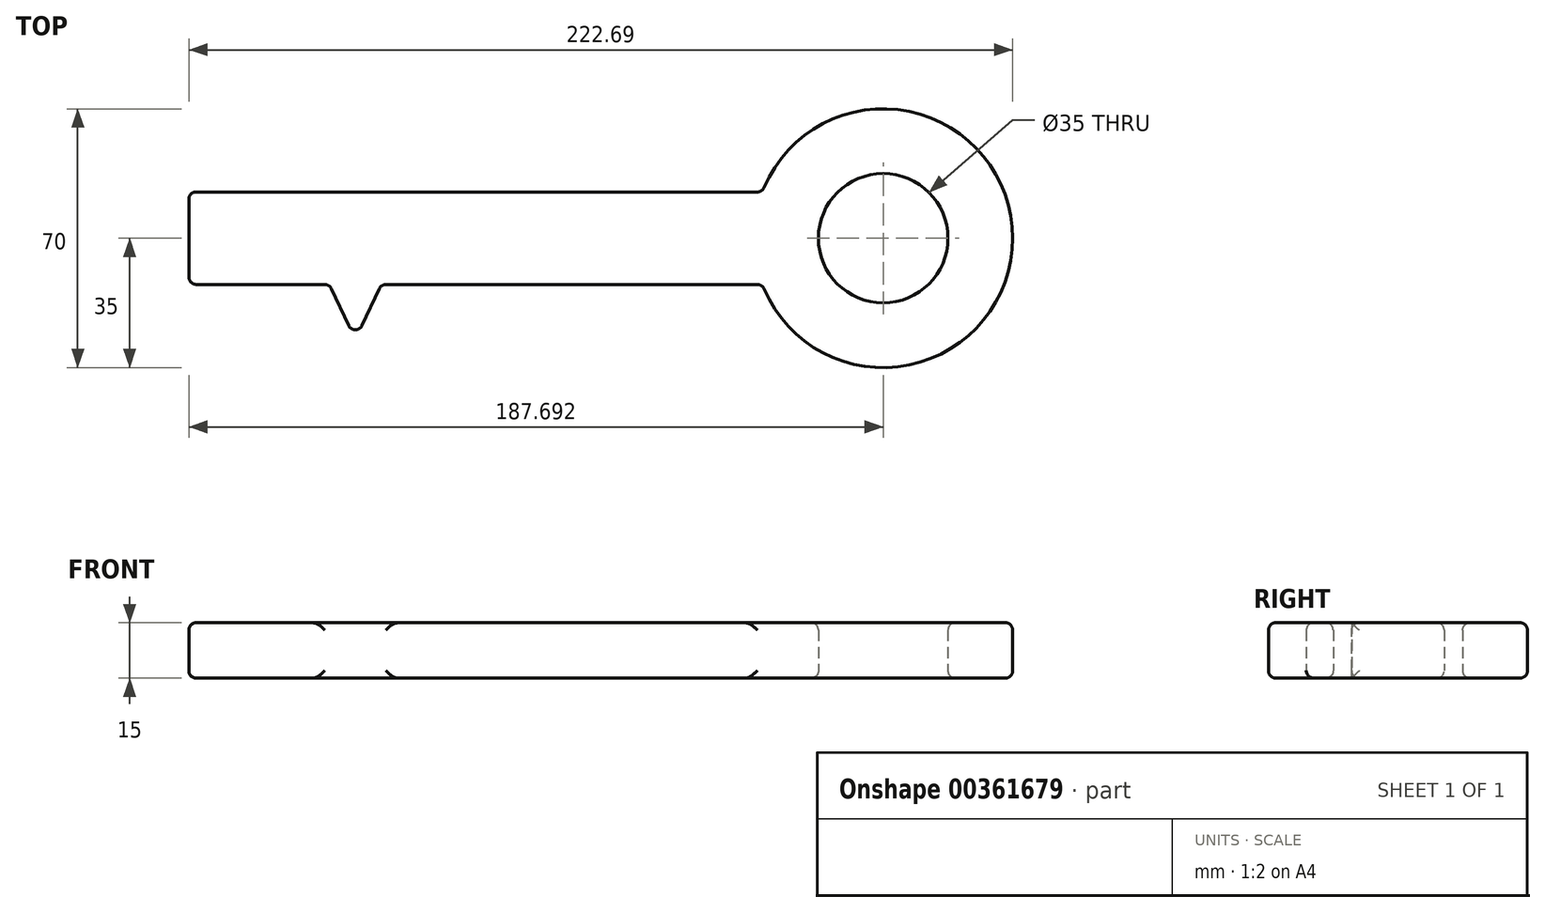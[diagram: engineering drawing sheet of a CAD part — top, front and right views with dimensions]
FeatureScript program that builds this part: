
annotation { "Feature Type Name" : "Feature", "Feature Type Description" : "" }
export const myFeature = defineFeature(function(context is Context, id is Id, definition is map)
    precondition{}
    {
        {
            var Q0;
            Q0=qCreatedBy(makeId("Top.planeOp"),FACE);
            var sketch = newSketch(context, id + "F0", { "sketchPlane" : qUnion([Q0])});
            skLineSegment(sketch, "E0.bottom", {"start": v(-10, 14.65) * mm, "end": v(145, 14.65) * mm});
            skLineSegment(sketch, "E0.top", {"start": v(-10, -10.35) * mm, "end": v(145, -10.35) * mm});
            skLineSegment(sketch, "E0.left", {"start": v(-10, 14.65) * mm, "end": v(-10, -10.35) * mm});
            skLineSegment(sketch, "E1.bottom", {"start": v(0, -10.35) * mm, "end": v(-10, -10.35) * mm});
            skLineSegment(sketch, "E1.top", {"start": v(0, -40.35) * mm, "end": v(-10, -40.35) * mm});
            skLineSegment(sketch, "E1.left", {"start": v(-10, -40.35) * mm, "end": v(-10, -10.35) * mm});
            skLineSegment(sketch, "E1.right", {"start": v(0, -40.35) * mm, "end": v(0, -10.35) * mm});
            skLineSegment(sketch, "E2.top", {"start": v(0, -10.35) * mm, "end": v(145, -10.35) * mm});
            skLineSegment(sketch, "E3.bottom", {"start": v(10, -10.35) * mm, "end": v(18, -10.35) * mm});
            skLineSegment(sketch, "E3.top", {"start": v(10, -10.35) * mm, "end": v(18, -10.35) * mm});
            skLineSegment(sketch, "E3.left", {"start": v(10, -10.35) * mm, "end": v(10, -10.35) * mm});
            skLineSegment(sketch, "E3.right", {"start": v(18, -10.35) * mm, "end": v(18, -10.35) * mm});
            skLineSegment(sketch, "E4.top", {"start": v(10, -25.35) * mm, "end": v(18, -25.35) * mm});
            skLineSegment(sketch, "E4.left", {"start": v(10, -10.35) * mm, "end": v(10, -25.35) * mm});
            skLineSegment(sketch, "E4.right", {"start": v(18, -10.35) * mm, "end": v(18, -25.35) * mm});
            skLineSegment(sketch, "E5", {"start": v(28, -10.35) * mm, "end": v(35, -25.35) * mm});
            skLineSegment(sketch, "E6", {"start": v(35, -25.35) * mm, "end": v(42, -10.35) * mm});
            skArc(sketch, "E7", {"start": v(145, -10.35) * mm, "mid": v(212.7, 2.15) * mm, "end": v(145, 14.65) * mm});
            skCircle(sketch, "E8", {"center": v(177.7, 2.15) * mm, "radius": 17.5 * mm});
            skLineSegment(sketch, "E9", {"start": v(177.7, 2.15) * mm, "end": v(-10, 2.15) * mm, "construction": true});
            skSolve(sketch);
        }
        {
            var Q0;
            {var subQ0=sQuery(id+"F0.wireOp",EDGE,"E5");Q0=makeQuery(id+"F0.imprint","IMPRINT",FACE,{"disambiguationData":[TD([[makeQuery(id+"F0.imprint","IMPRINT",EDGE,{"derivedFrom":subQ0}),1.0]])]});}
            var Q1;
            Q1=makeQuery(id+"F0.imprint","IMPRINT",FACE,{"disambiguationData":[TD([[makeQuery(id+"F0.imprint","IMPRINT",EDGE,{"derivedFrom":sQuery(id+"F0.wireOp",EDGE,"E1.bottom")}),1.0]])]});
            var Q2;
            Q2=makeQuery(id+"F0.imprint","IMPRINT",FACE,{"disambiguationData":[TD([[makeQuery(id+"F0.imprint","IMPRINT",EDGE,{"derivedFrom":sQuery(id+"F0.wireOp",EDGE,"E0.bottom")}),-1.0]])]});
            var Q3;
            Q3=makeQuery(id+"F0.imprint","IMPRINT",FACE,{"disambiguationData":[TD([[makeQuery(id+"F0.imprint","IMPRINT",EDGE,{"derivedFrom":sQuery(id+"F0.wireOp",EDGE,"E3.bottom")}),-1.0]])]});
            extrude(context, id + "F1", {"entities" : qUnion([Q0, Q1, Q2, Q3]), "depth" : 15 * mm});
        }
        {
            var Q0;
            Q0=makeQuery(id+"F1.opExtrude","CAP_EDGE",EDGE,{"disambiguationData":[OSD([sQuery(id+"F0.wireOp",EDGE,"E6")])],"isStart":true});
            var Q1;
            Q1=makeQuery(id+"F1.opExtrude","CAP_EDGE",EDGE,{"disambiguationData":[OSD([sQuery(id+"F0.wireOp",EDGE,"E8")])],"isStart":true});
            var Q2;
            Q2=makeQuery(id+"F1.opExtrude","CAP_EDGE",EDGE,{"disambiguationData":[OSD([sQuery(id+"F0.wireOp",EDGE,"E5")])],"isStart":true});
            var Q3;
            {var subQ0=sQuery(id+"F0.wireOp",EDGE,"E2.top");Q3=makeQuery(id+"F1.opExtrude","CAP_EDGE",EDGE,{"disambiguationData":[OSD([subQ0]),TDD([makeQuery(id+"F0.imprint","IMPRINT",EDGE,{"disambiguationData":[TD([[makeQuery(id+"F0.imprint","INTERSECT",VERTEX,{"derivedFrom":[subQ0,sQuery(id+"F0.wireOp",EDGE,"E5")]}),1.0]])],"derivedFrom":subQ0})])],"isStart":true});}
            var Q4;
            Q4=makeQuery(id+"F1.opExtrude","SWEPT_EDGE",EDGE,{"disambiguationData":[OSD([sQuery(id+"F0.wireOp",EDGE,"E2.top"),sQuery(id+"F0.wireOp",EDGE,"E5")])]});
            var Q5;
            Q5=makeQuery(id+"F1.opExtrude","CAP_EDGE",EDGE,{"disambiguationData":[OSD([sQuery(id+"F0.wireOp",EDGE,"E4.top")])],"isStart":true});
            var Q6;
            {var subQ0=sQuery(id+"F0.wireOp",EDGE,"E2.top");Q6=makeQuery(id+"F1.opExtrude","CAP_EDGE",EDGE,{"disambiguationData":[OSD([subQ0]),TDD([makeQuery(id+"F0.imprint","IMPRINT",EDGE,{"disambiguationData":[TD([[makeQuery(id+"F0.imprint","INTERSECT",VERTEX,{"derivedFrom":[subQ0,sQuery(id+"F0.wireOp",EDGE,"E7")]}),1.0]])],"derivedFrom":subQ0})])],"isStart":true});}
            var Q7;
            Q7=makeQuery(id+"F1.opExtrude","CAP_EDGE",EDGE,{"disambiguationData":[OSD([sQuery(id+"F0.wireOp",EDGE,"E8")])],"isStart":false});
            var Q8;
            Q8=makeQuery(id+"F1.opExtrude","SWEPT_EDGE",EDGE,{"disambiguationData":[OSD([sQuery(id+"F0.wireOp",EDGE,"E2.top"),sQuery(id+"F0.wireOp",EDGE,"E6")])]});
            var Q9;
            Q9=makeQuery(id+"F1.opExtrude","CAP_EDGE",EDGE,{"disambiguationData":[OSD([sQuery(id+"F0.wireOp",EDGE,"E1.right")])],"isStart":true});
            var Q10;
            Q10=makeQuery(id+"F1.opExtrude","CAP_EDGE",EDGE,{"disambiguationData":[OSD([sQuery(id+"F0.wireOp",EDGE,"E4.right")])],"isStart":true});
            var Q11;
            Q11=makeQuery(id+"F1.opExtrude","SWEPT_EDGE",EDGE,{"disambiguationData":[OSD([sQuery(id+"F0.wireOp",EDGE,"E5"),sQuery(id+"F0.wireOp",EDGE,"E6")])]});
            var Q12;
            Q12=makeQuery(id+"F1.opExtrude","SWEPT_EDGE",EDGE,{"disambiguationData":[OSD([sQuery(id+"F0.wireOp",EDGE,"E2.top"),sQuery(id+"F0.wireOp",EDGE,"E3.bottom"),sQuery(id+"F0.wireOp",EDGE,"E4.left")])]});
            var Q13;
            Q13=makeQuery(id+"F1.opExtrude","SWEPT_EDGE",EDGE,{"disambiguationData":[OSD([sQuery(id+"F0.wireOp",EDGE,"E1.bottom"),sQuery(id+"F0.wireOp",EDGE,"E1.right"),sQuery(id+"F0.wireOp",EDGE,"E2.top")])]});
            var Q14;
            Q14=makeQuery(id+"F1.opExtrude","CAP_EDGE",EDGE,{"disambiguationData":[OSD([sQuery(id+"F0.wireOp",EDGE,"E6")])],"isStart":false});
            var Q15;
            Q15=makeQuery(id+"F1.opExtrude","SWEPT_EDGE",EDGE,{"disambiguationData":[OSD([sQuery(id+"F0.wireOp",EDGE,"E2.top"),sQuery(id+"F0.wireOp",EDGE,"E7")])]});
            var Q16;
            Q16=makeQuery(id+"F1.opExtrude","CAP_EDGE",EDGE,{"disambiguationData":[OSD([sQuery(id+"F0.wireOp",EDGE,"E0.bottom")])],"isStart":true});
            var Q17;
            Q17=makeQuery(id+"F1.opExtrude","SWEPT_EDGE",EDGE,{"disambiguationData":[OSD([sQuery(id+"F0.wireOp",EDGE,"E4.top"),sQuery(id+"F0.wireOp",EDGE,"E4.right")])]});
            var Q18;
            Q18=makeQuery(id+"F1.opExtrude","SWEPT_EDGE",EDGE,{"disambiguationData":[OSD([sQuery(id+"F0.wireOp",EDGE,"E4.top"),sQuery(id+"F0.wireOp",EDGE,"E4.left")])]});
            var Q19;
            Q19=makeQuery(id+"F1.opExtrude","SWEPT_EDGE",EDGE,{"disambiguationData":[OSD([sQuery(id+"F0.wireOp",EDGE,"E2.top"),sQuery(id+"F0.wireOp",EDGE,"E3.bottom"),sQuery(id+"F0.wireOp",EDGE,"E4.right")])]});
            var Q20;
            {var subQ0=sQuery(id+"F0.wireOp",EDGE,"E2.top");Q20=makeQuery(id+"F1.opExtrude","CAP_EDGE",EDGE,{"disambiguationData":[OSD([subQ0]),TDD([makeQuery(id+"F0.imprint","IMPRINT",EDGE,{"disambiguationData":[TD([[makeQuery(id+"F0.imprint","INTERSECT",VERTEX,{"derivedFrom":[sQuery(id+"F0.wireOp",EDGE,"E1.bottom"),sQuery(id+"F0.wireOp",EDGE,"E1.right"),subQ0]}),-1.0]])],"derivedFrom":subQ0})])],"isStart":true});}
            var Q21;
            Q21=makeQuery(id+"F1.opExtrude","CAP_EDGE",EDGE,{"disambiguationData":[OSD([sQuery(id+"F0.wireOp",EDGE,"E4.left")])],"isStart":true});
            var Q22;
            Q22=makeQuery(id+"F1.opExtrude","SWEPT_EDGE",EDGE,{"disambiguationData":[OSD([sQuery(id+"F0.wireOp",EDGE,"E1.top"),sQuery(id+"F0.wireOp",EDGE,"E1.right")])]});
            var Q23;
            Q23=makeQuery(id+"F1.opExtrude","CAP_EDGE",EDGE,{"disambiguationData":[OSD([sQuery(id+"F0.wireOp",EDGE,"E0.left"),sQuery(id+"F0.wireOp",EDGE,"E1.left")])],"isStart":true});
            var Q24;
            Q24=makeQuery(id+"F1.opExtrude","CAP_EDGE",EDGE,{"disambiguationData":[OSD([sQuery(id+"F0.wireOp",EDGE,"E1.top")])],"isStart":true});
            var Q25;
            Q25=makeQuery(id+"F1.opExtrude","CAP_EDGE",EDGE,{"disambiguationData":[OSD([sQuery(id+"F0.wireOp",EDGE,"E5")])],"isStart":false});
            var Q26;
            Q26=makeQuery(id+"F1.opExtrude","SWEPT_EDGE",EDGE,{"disambiguationData":[OSD([sQuery(id+"F0.wireOp",EDGE,"E0.bottom"),sQuery(id+"F0.wireOp",EDGE,"E7")])]});
            var Q27;
            Q27=makeQuery(id+"F1.opExtrude","CAP_EDGE",EDGE,{"disambiguationData":[OSD([sQuery(id+"F0.wireOp",EDGE,"E0.left"),sQuery(id+"F0.wireOp",EDGE,"E1.left")])],"isStart":false});
            var Q28;
            Q28=makeQuery(id+"F1.opExtrude","CAP_EDGE",EDGE,{"disambiguationData":[OSD([sQuery(id+"F0.wireOp",EDGE,"E1.right")])],"isStart":false});
            var Q29;
            {var subQ0=sQuery(id+"F0.wireOp",EDGE,"E2.top");Q29=makeQuery(id+"F1.opExtrude","CAP_EDGE",EDGE,{"disambiguationData":[OSD([subQ0]),TDD([makeQuery(id+"F0.imprint","IMPRINT",EDGE,{"disambiguationData":[TD([[makeQuery(id+"F0.imprint","INTERSECT",VERTEX,{"derivedFrom":[subQ0,sQuery(id+"F0.wireOp",EDGE,"E7")]}),1.0]])],"derivedFrom":subQ0})])],"isStart":false});}
            var Q30;
            Q30=makeQuery(id+"F1.opExtrude","CAP_EDGE",EDGE,{"disambiguationData":[OSD([sQuery(id+"F0.wireOp",EDGE,"E4.top")])],"isStart":false});
            var Q31;
            Q31=makeQuery(id+"F1.opExtrude","CAP_EDGE",EDGE,{"disambiguationData":[OSD([sQuery(id+"F0.wireOp",EDGE,"E4.right")])],"isStart":false});
            var Q32;
            Q32=makeQuery(id+"F1.opExtrude","CAP_EDGE",EDGE,{"disambiguationData":[OSD([sQuery(id+"F0.wireOp",EDGE,"E4.left")])],"isStart":false});
            var Q33;
            {var subQ0=sQuery(id+"F0.wireOp",EDGE,"E2.top");Q33=makeQuery(id+"F1.opExtrude","CAP_EDGE",EDGE,{"disambiguationData":[OSD([subQ0]),TDD([makeQuery(id+"F0.imprint","IMPRINT",EDGE,{"disambiguationData":[TD([[makeQuery(id+"F0.imprint","INTERSECT",VERTEX,{"derivedFrom":[sQuery(id+"F0.wireOp",EDGE,"E1.bottom"),sQuery(id+"F0.wireOp",EDGE,"E1.right"),subQ0]}),-1.0]])],"derivedFrom":subQ0})])],"isStart":false});}
            var Q34;
            Q34=makeQuery(id+"F1.opExtrude","SWEPT_EDGE",EDGE,{"disambiguationData":[OSD([sQuery(id+"F0.wireOp",EDGE,"E1.top"),sQuery(id+"F0.wireOp",EDGE,"E1.left")])]});
            var Q35;
            {var subQ0=sQuery(id+"F0.wireOp",EDGE,"E2.top");Q35=makeQuery(id+"F1.opExtrude","CAP_EDGE",EDGE,{"disambiguationData":[OSD([subQ0]),TDD([makeQuery(id+"F0.imprint","IMPRINT",EDGE,{"disambiguationData":[TD([[makeQuery(id+"F0.imprint","INTERSECT",VERTEX,{"derivedFrom":[subQ0,sQuery(id+"F0.wireOp",EDGE,"E5")]}),1.0]])],"derivedFrom":subQ0})])],"isStart":false});}
            var Q36;
            Q36=makeQuery(id+"F1.opExtrude","SWEPT_EDGE",EDGE,{"disambiguationData":[OSD([sQuery(id+"F0.wireOp",EDGE,"E0.bottom"),sQuery(id+"F0.wireOp",EDGE,"E0.left")])]});
            var Q37;
            Q37=makeQuery(id+"F1.opExtrude","CAP_EDGE",EDGE,{"disambiguationData":[OSD([sQuery(id+"F0.wireOp",EDGE,"E0.bottom")])],"isStart":false});
            var Q38;
            Q38=makeQuery(id+"F1.opExtrude","CAP_EDGE",EDGE,{"disambiguationData":[OSD([sQuery(id+"F0.wireOp",EDGE,"E1.top")])],"isStart":false});
            var Q39;
            Q39=makeQuery(id+"F1.opExtrude","CAP_EDGE",EDGE,{"disambiguationData":[OSD([sQuery(id+"F0.wireOp",EDGE,"E7")])],"isStart":true});
            var Q40;
            Q40=makeQuery(id+"F1.opExtrude","CAP_EDGE",EDGE,{"disambiguationData":[OSD([sQuery(id+"F0.wireOp",EDGE,"E7")])],"isStart":false});
            fillet(context, id + "F2", {"entities" : qUnion([Q0, Q1, Q2, Q3, Q4, Q5, Q6, Q7, Q8, Q9, Q10, Q11, Q12, Q13, Q14, Q15, Q16, Q17, Q18, Q19, Q20, Q21, Q22, Q23, Q24, Q25, Q26, Q27, Q28, Q29, Q30, Q31, Q32, Q33, Q34, Q35, Q36, Q37, Q38, Q39, Q40]), "radius" : 2 * mm, "tangentPropagation" : true, "allowEdgeOverflow" : false});
        }
    });
